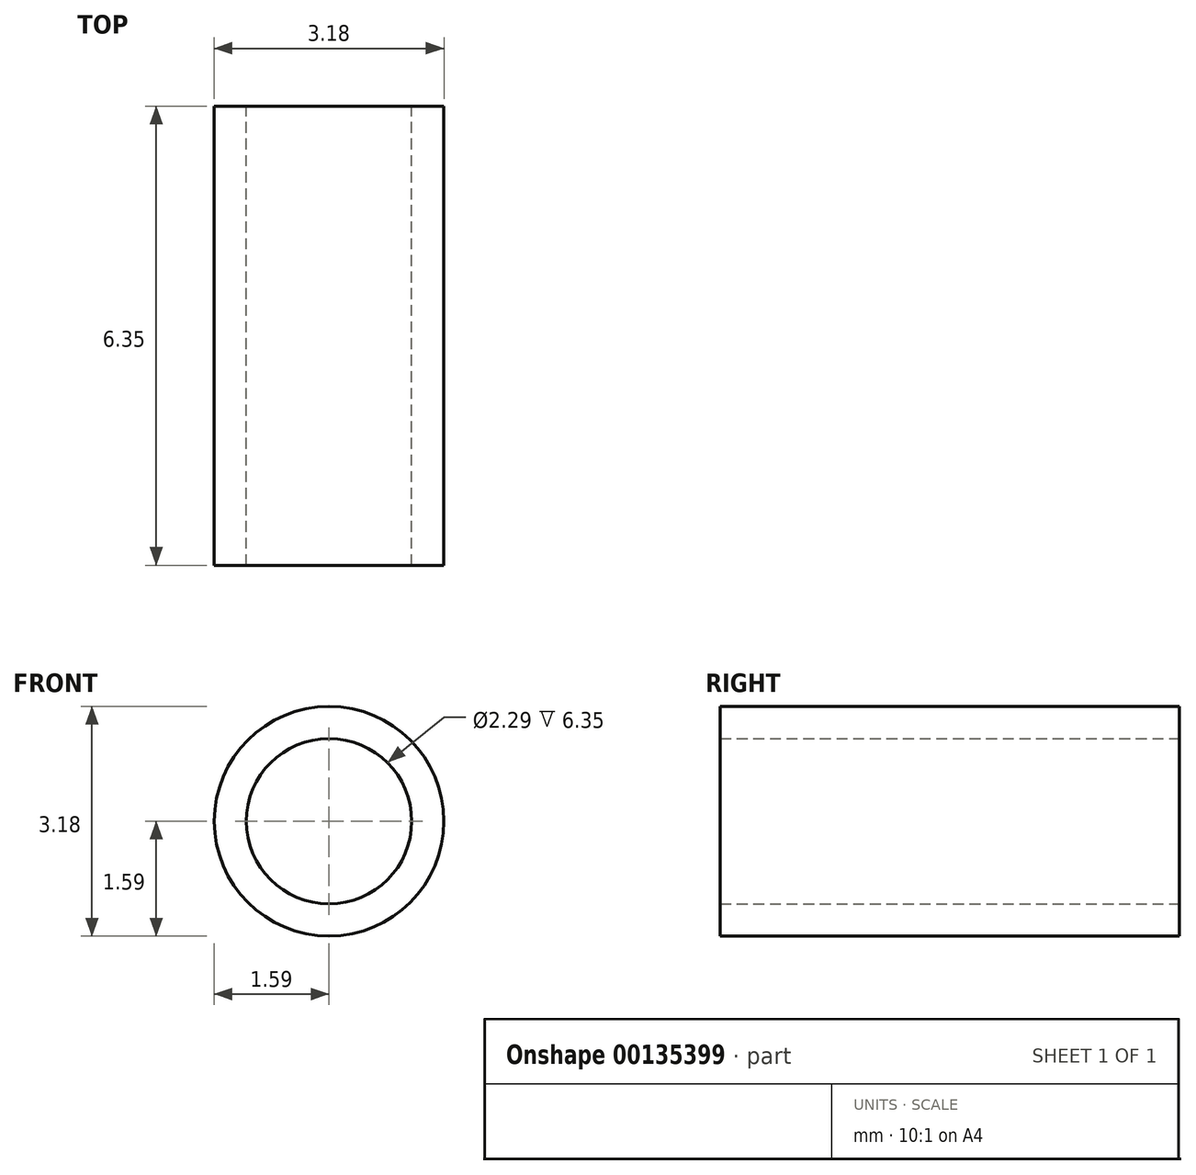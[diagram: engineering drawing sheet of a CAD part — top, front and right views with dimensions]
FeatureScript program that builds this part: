
annotation { "Feature Type Name" : "Feature", "Feature Type Description" : "" }
export const myFeature = defineFeature(function(context is Context, id is Id, definition is map)
    precondition{}
    {
        {
            var Q0;
            Q0=qCreatedBy(makeId("Front.planeOp"),FACE);
            var sketch = newSketch(context, id + "F0", { "sketchPlane" : qUnion([Q0])});
            skCircle(sketch, "E0", {"center": v(0, 0) * mm, "radius": 1.14 * mm});
            skCircle(sketch, "E1", {"center": v(0, 0) * mm, "radius": 1.59 * mm});
            skSolve(sketch);
        }
        {
            var Q0;
            Q0=makeQuery(id+"F0.imprint","IMPRINT",FACE,{"disambiguationData":[TD([[makeQuery(id+"F0.imprint","IMPRINT",EDGE,{"derivedFrom":sQuery(id+"F0.wireOp",EDGE,"E0")}),-1.0]])]});
            extrude(context, id + "F1", {"entities" : qUnion([Q0]), "depth" : 6.35 * mm});
        }
    });
